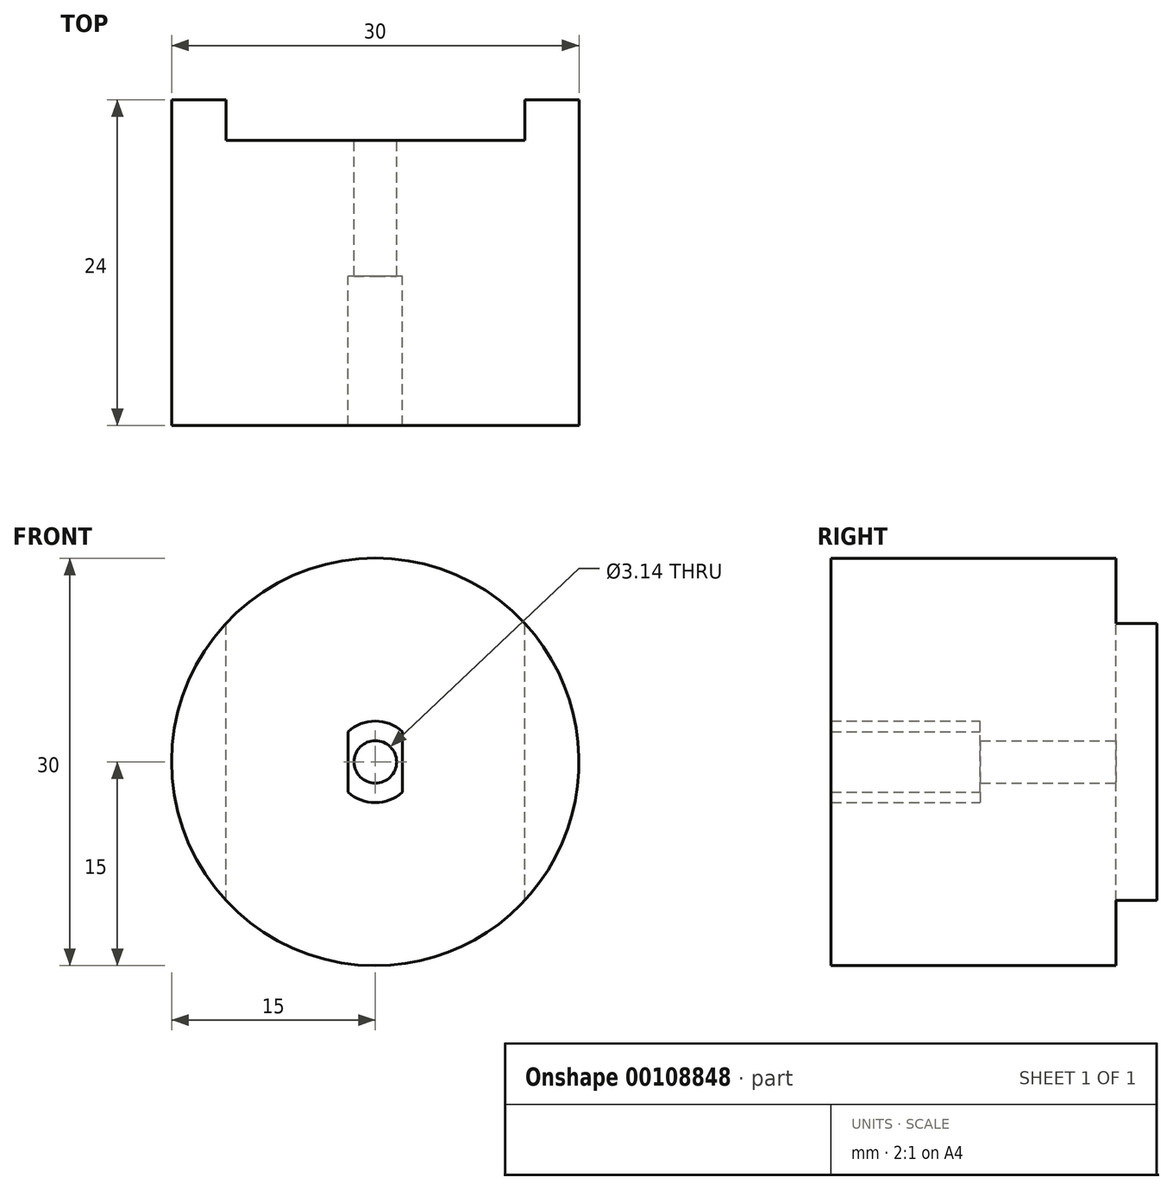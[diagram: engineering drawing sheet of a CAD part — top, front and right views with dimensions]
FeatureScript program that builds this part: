
annotation { "Feature Type Name" : "Feature", "Feature Type Description" : "" }
export const myFeature = defineFeature(function(context is Context, id is Id, definition is map)
    precondition{}
    {
        {
            var Q0;
            Q0=qCreatedBy(makeId("Front.planeOp"),FACE);
            var sketch = newSketch(context, id + "F0", { "sketchPlane" : qUnion([Q0])});
            skArc(sketch, "E0", {"start": v(-2, -2.24) * mm, "mid": v(0, -3) * mm, "end": v(2, -2.24) * mm});
            skCircle(sketch, "E1", {"center": v(0, 0) * mm, "radius": 15 * mm});
            skLineSegment(sketch, "E2", {"start": v(-2, 2.24) * mm, "end": v(-2, -2.24) * mm});
            skLineSegment(sketch, "E3", {"start": v(2, 2.24) * mm, "end": v(2, -2.24) * mm});
            skLineSegment(sketch, "E4", {"start": v(0, 5.07) * mm, "end": v(0, -4.03) * mm, "construction": true});
            skArc(sketch, "E5.trimOffspring", {"start": v(2, 2.24) * mm, "mid": v(0, 3) * mm, "end": v(-2, 2.24) * mm});
            skSolve(sketch);
        }
        {
            var Q0;
            Q0=makeQuery(id+"F0.imprint","IMPRINT",FACE,{"disambiguationData":[TD([[makeQuery(id+"F0.imprint","IMPRINT",EDGE,{"derivedFrom":sQuery(id+"F0.wireOp",EDGE,"E0")}),-1.0]])]});
            extrude(context, id + "F1", {"entities" : qUnion([Q0]), "depth" : 24 * mm});
        }
        {
            var Q0;
            Q0=qCreatedBy(makeId("Top.planeOp"),FACE);
            var sketch = newSketch(context, id + "F2", { "sketchPlane" : qUnion([Q0])});
            skPoint(sketch, "E6.endSnap0", {"position": v(-0.14, -20.8) * mm});
            skLineSegment(sketch, "E7.bottom", {"start": v(-11, 0) * mm, "end": v(0, 0) * mm});
            skLineSegment(sketch, "E7.top", {"start": v(-11, -3) * mm, "end": v(0, -3) * mm});
            skLineSegment(sketch, "E7.left", {"start": v(-11, 0) * mm, "end": v(-11, -3) * mm});
            skLineSegment(sketch, "E7.right", {"start": v(0, 0) * mm, "end": v(0, -3) * mm});
            skLineSegment(sketch, "E8", {"start": v(0, 9.86) * mm, "end": v(0, -28) * mm, "construction": true});
            skLineSegment(sketch, "E9.MirrorCS", {"start": v(11, 0) * mm, "end": v(0, 0) * mm});
            skLineSegment(sketch, "E10.MirrorCS", {"start": v(11, 0) * mm, "end": v(11, -3) * mm});
            skLineSegment(sketch, "E11.MirrorCS", {"start": v(11, -3) * mm, "end": v(0, -3) * mm});
            skSolve(sketch);
        }
        {
            var Q0;
            Q0 = qSketchRegion(id + "F2", true);
            extrude(context, id + "F3", {"entities" : qUnion([Q0]), "operationType" : NewBodyOperationType.REMOVE, "endBound" : BoundingType.SYMMETRIC, "oppositeDirection" : true, "depth" : 30 * mm});
        }
        {
            var Q0;
            Q0=makeQuery(id+"F3.boolean.opBoolean","COPY",FACE,{"derivedFrom":makeQuery(id+"F3.opExtrude","SWEPT_FACE",FACE,{"disambiguationData":[OSD([sQuery(id+"F2.wireOp",EDGE,"E7.top"),sQuery(id+"F2.wireOp",EDGE,"E11.MirrorCS")])]})});
            cPlane(context, id + "F4", {"entities" : qUnion([Q0]), "cplaneType" : CPlaneType.OFFSET, "offset" : 0 * mm, "width" : 150 * mm, "height" : 150 * mm});
        }
        {
            var Q0;
            Q0=qCreatedBy(id+"F4.planeOp",FACE);
            var sketch = newSketch(context, id + "F5", { "sketchPlane" : qUnion([Q0])});
            skCircle(sketch, "E12", {"center": v(0, 0) * mm, "radius": 1.57 * mm});
            skCircle(sketch, "E13", {"center": v(0, 0) * mm, "radius": 3.06 * mm});
            skSolve(sketch);
        }
        {
            var Q0;
            Q0 = qSketchRegion(id + "F5", true);
            extrude(context, id + "F6", {"entities" : qUnion([Q0]), "operationType" : NewBodyOperationType.ADD, "oppositeDirection" : true, "depth" : 10 * mm});
        }
    });
